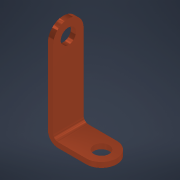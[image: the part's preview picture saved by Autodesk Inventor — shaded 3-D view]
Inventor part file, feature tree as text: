
AUTODESK INVENTOR PART (.ipt)
format: ipt  version: 2022 (Build 260153000, 153)  size: 136,704 bytes
history: native  units: mm
features: sheet_metal_op x3, sketch x3, hole x2, chamfer x1, other x1, projected_geometry x1
ambient origin geometry x8: Origin, YZ Plane, XZ Plane, XY Plane, X Axis, Y Axis, Z Axis, Center Point
bodies: Solid1 (feature_tree)
feature tree (11):
  sheet_metal_op  "Contour Flange1"
  chamfer  "Corner Round1"
  hole  "Hole1"  [1 undecoded]
  hole  "Hole2"  [1 undecoded]
  sketch  "Sketch1"  dims[d0=10.5mm d1=20.0mm]
  other  "Plate1"
  sheet_metal_op  "Bend1"
  sheet_metal_op  "Corner1"
  sketch  "Sketch2"  dims[d2=1.0mm d3=1.0mm]
  projected_geometry  "Projected Loop1"
  sketch  "Sketch3"  dims[d4=0.5mm d5=2.0mm d6=1.0mm d7=6.0mm d8=1.0mm d9=1.0mm d10=4.0mm d11=1.0mm d12=1.0mm d13=3.0mm d14=3.0mm d15=6.0mm d16=4.0mm d17=2.0mm d18=90.0deg d19=1.0mm d20=20.594885mm d21=3.0mm d22=6.0mm d23=4.0mm d24=2.0mm d25=90.0deg d26=8.0mm d27=20.594885mm]
note: 2 required parameter values undecoded (feature->parameter linkage not recoverable at this tier; creation-order binding heuristic only, values carry confidence <= 0.55)
